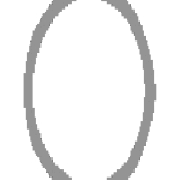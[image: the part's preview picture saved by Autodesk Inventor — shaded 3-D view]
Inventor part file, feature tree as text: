
AUTODESK INVENTOR PART (.ipt)
format: ipt  version: 2021 (Build 250183000, 183)  size: 138,240 bytes
history: native  units: in
note: dims shown in document units (in); Inventor stores cm internally (conversion verified against a paired STEP export)
features: plane x7, sketch x5, other x4, extrude x2, boolean_combine x2
ambient origin geometry x8: Origin, YZ Plane, XZ Plane, XY Plane, X Axis, Y Axis, Z Axis, Center Point
bodies: Solid1 (feature_tree), Body (feature_tree), Solid2 (feature_tree), Solid3 (feature_tree)
feature tree (20):
  other  "Driven Length"
  other  "Frame Generator"
  other  "Start Plane"
  other  "End Plane"
  plane  "Work Plane4"
  plane  "Work Plane5"
  plane  "Work Plane6"
  extrude  "Extrusion3"  Depth=0.065in
  boolean_combine  "Combine1"
  plane  "Work Plane7"
  plane  "Work Plane8"
  plane  "Work Plane9"
  extrude  "Extrusion4"  TaperAngle=0.0deg  [1 undecoded]
  boolean_combine  "Combine2"
  sketch  "Sketch"  dims[d8=90.0deg d9=14.625in d10=0.12in d11=0.0in d12=0.12in d13=0.0in]
  sketch  "Sketch2"  dims[d0=1.0in d1=0.065in]
  plane  "Work Plane3"
  sketch  "Sketch3"  dims[d2=14.625in d4=-0.0in]
  sketch  "Sketch4"  dims[d5=14.625in]
  sketch  "Sketch5"  dims[d6=0.12in d7=0.0in]
note: 1 required parameter value undecoded (feature->parameter linkage not recoverable at this tier; creation-order binding heuristic only, values carry confidence <= 0.55)
